# Revit family: MF consegna 01 tavolo lampada
name_source: partatom
category: Apparecchi per illuminazione
revit_build: Autodesk Revit 2013 (Build: 20120221_2030(x64)
units: mm (PartAtom-declared; Revit-internal decimal feet)

## types (2) — shared parameters
Filtro dei colori = 16777215
Materiale base = Plastica, Bianco opaco
Spessore paralume = 1 cm
Variazione temperatura colore lampada con luminosità attenuata = <Nessuno>

## per-type parameters (varying)
| type | Dimensioni simbolo sorgente d'illuminazione | H Lampada | H paralume | H ripiano | Materiale paralume | Raggio base | Raggio inferiore montante | Raggio inferiore paralume | Raggio ripiano | Raggio superiore montante | Raggio superiore paralume | Spessore base/ripiano esterno | Spessore base/ripiano interno |
| Lampada h 160cm - tessuto azzurro | 25 cm | 160 cm | 50 cm | 70 cm | Lino - Azzurro | 30 cm | 5 cm | 39 cm | 42 cm | 3 cm | 30 cm | 2 cm | 4 cm |
| Lampada h 80 cm - tessuto rosso | 13 cm | 80 cm | 25 cm | 30 cm | Lino - Rosso | 20 cm | 3 cm | 22 cm | 27 cm | 1 cm | 20 cm | 1 cm | 2 cm |

## geometry (parser evidence)
native form markers: Blend x8
no freeform markers — native parametric forms only
